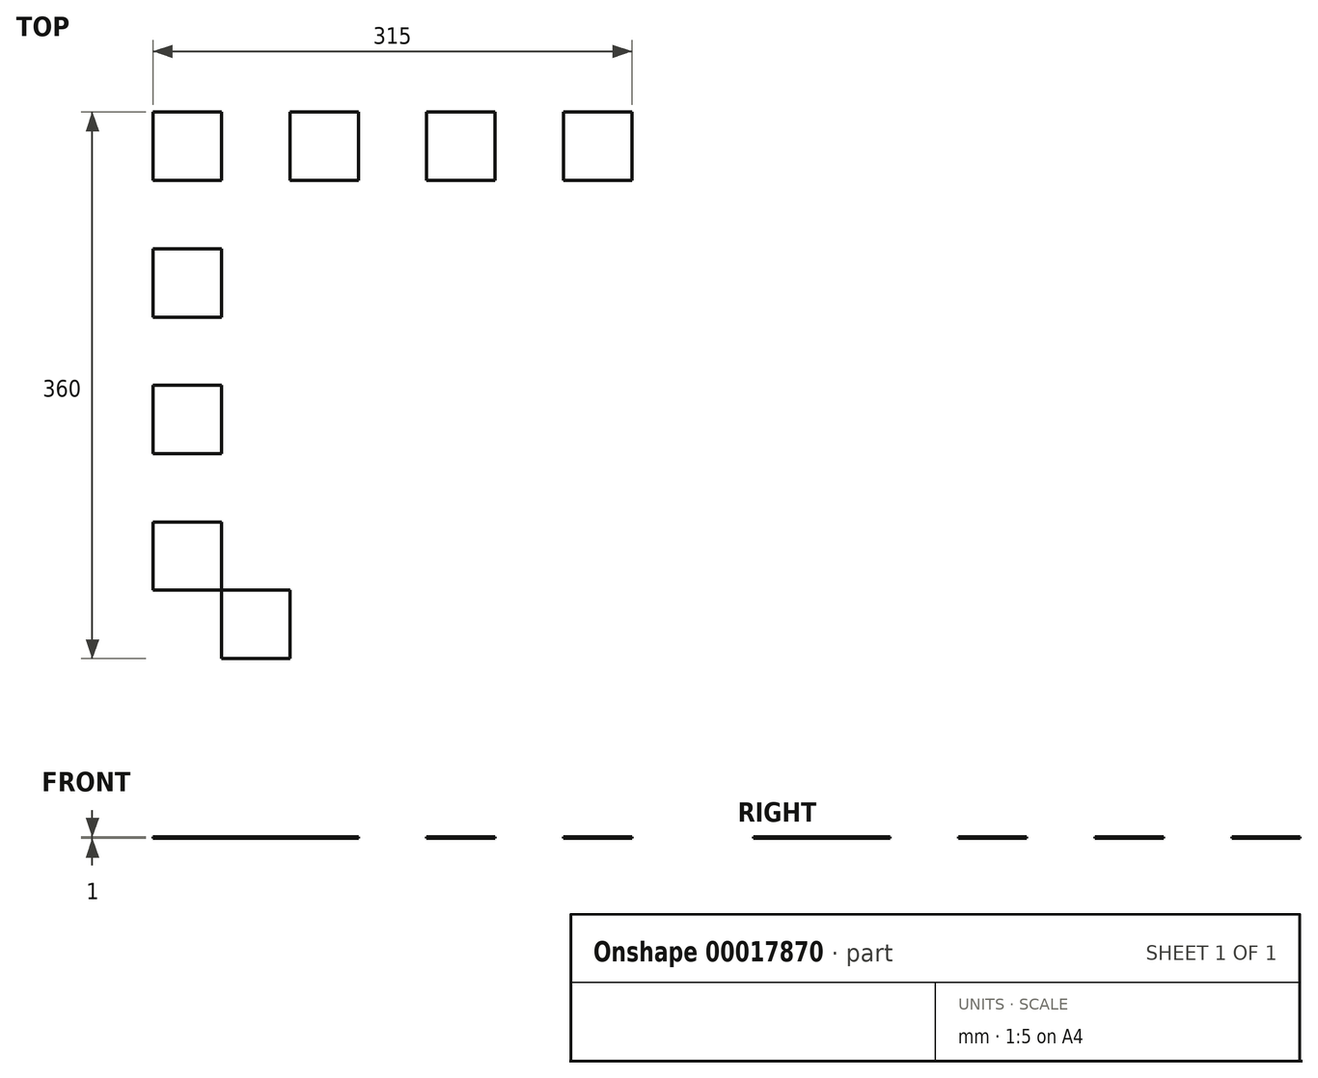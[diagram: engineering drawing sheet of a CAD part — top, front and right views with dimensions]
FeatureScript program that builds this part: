
annotation { "Feature Type Name" : "Feature", "Feature Type Description" : "" }
export const myFeature = defineFeature(function(context is Context, id is Id, definition is map)
    precondition{}
    {
        {
            var Q0;
            Q0=qCreatedBy(makeId("Top.planeOp"),FACE);
            var sketch = newSketch(context, id + "F0", { "sketchPlane" : qUnion([Q0])});
            skLineSegment(sketch, "E0.bottom", {"start": v(0, 0) * mm, "end": v(25.4, 0) * mm});
            skLineSegment(sketch, "E0.top", {"start": v(0, 25.4) * mm, "end": v(25.4, 25.4) * mm});
            skLineSegment(sketch, "E0.left", {"start": v(0, 0) * mm, "end": v(0, 25.4) * mm});
            skLineSegment(sketch, "E0.right", {"start": v(25.4, 0) * mm, "end": v(25.4, 25.4) * mm});
            skSolve(sketch);
        }
        {
            var Q0;
            Q0=qCreatedBy(makeId("Top.planeOp"),FACE);
            var sketch = newSketch(context, id + "F1", { "sketchPlane" : qUnion([Q0])});
            skLineSegment(sketch, "E1.bottom", {"start": v(-9.8, -9.8) * mm, "end": v(35.2, -9.8) * mm});
            skLineSegment(sketch, "E1.top", {"start": v(-9.8, 35.2) * mm, "end": v(35.2, 35.2) * mm});
            skLineSegment(sketch, "E1.left", {"start": v(-9.8, -9.8) * mm, "end": v(-9.8, 35.2) * mm});
            skLineSegment(sketch, "E1.right", {"start": v(35.2, -9.8) * mm, "end": v(35.2, 35.2) * mm});
            skLineSegment(sketch, "E2.0.1.0", {"start": v(-9.8, 80.2) * mm, "end": v(35.2, 80.2) * mm});
            skLineSegment(sketch, "E2.0.1.1", {"start": v(-9.8, 35.2) * mm, "end": v(-9.8, 80.2) * mm});
            skLineSegment(sketch, "E2.0.1.3", {"start": v(35.2, 35.2) * mm, "end": v(35.2, 80.2) * mm});
            skLineSegment(sketch, "E2.0.2.0", {"start": v(-9.8, 125.2) * mm, "end": v(35.2, 125.2) * mm});
            skLineSegment(sketch, "E2.0.2.1", {"start": v(-9.8, 80.2) * mm, "end": v(-9.8, 125.2) * mm});
            skLineSegment(sketch, "E2.0.2.2", {"start": v(-9.8, 80.2) * mm, "end": v(35.2, 80.2) * mm});
            skLineSegment(sketch, "E2.0.2.3", {"start": v(35.2, 80.2) * mm, "end": v(35.2, 125.2) * mm});
            skLineSegment(sketch, "E2.0.3.0", {"start": v(-9.8, 170.2) * mm, "end": v(35.2, 170.2) * mm});
            skLineSegment(sketch, "E2.0.3.1", {"start": v(-9.8, 125.2) * mm, "end": v(-9.8, 170.2) * mm});
            skLineSegment(sketch, "E2.0.3.2", {"start": v(-9.8, 125.2) * mm, "end": v(35.2, 125.2) * mm});
            skLineSegment(sketch, "E2.0.3.3", {"start": v(35.2, 125.2) * mm, "end": v(35.2, 170.2) * mm});
            skLineSegment(sketch, "E2.0.4.0", {"start": v(-9.8, 215.2) * mm, "end": v(35.2, 215.2) * mm});
            skLineSegment(sketch, "E2.0.4.1", {"start": v(-9.8, 170.2) * mm, "end": v(-9.8, 215.2) * mm});
            skLineSegment(sketch, "E2.0.4.2", {"start": v(-9.8, 170.2) * mm, "end": v(35.2, 170.2) * mm});
            skLineSegment(sketch, "E2.0.4.3", {"start": v(35.2, 170.2) * mm, "end": v(35.2, 215.2) * mm});
            skLineSegment(sketch, "E2.0.5.0", {"start": v(-9.8, 260.2) * mm, "end": v(35.2, 260.2) * mm});
            skLineSegment(sketch, "E2.0.5.1", {"start": v(-9.8, 215.2) * mm, "end": v(-9.8, 260.2) * mm});
            skLineSegment(sketch, "E2.0.5.2", {"start": v(-9.8, 215.2) * mm, "end": v(35.2, 215.2) * mm});
            skLineSegment(sketch, "E2.0.5.3", {"start": v(35.2, 215.2) * mm, "end": v(35.2, 260.2) * mm});
            skLineSegment(sketch, "E2.0.6.0", {"start": v(-9.8, 305.2) * mm, "end": v(35.2, 305.2) * mm});
            skLineSegment(sketch, "E2.0.6.1", {"start": v(-9.8, 260.2) * mm, "end": v(-9.8, 305.2) * mm});
            skLineSegment(sketch, "E2.0.6.2", {"start": v(-9.8, 260.2) * mm, "end": v(35.2, 260.2) * mm});
            skLineSegment(sketch, "E2.0.6.3", {"start": v(35.2, 260.2) * mm, "end": v(35.2, 305.2) * mm});
            skLineSegment(sketch, "E2.0.7.0", {"start": v(-9.8, 350.2) * mm, "end": v(35.2, 350.2) * mm});
            skLineSegment(sketch, "E2.0.7.1", {"start": v(-9.8, 305.2) * mm, "end": v(-9.8, 350.2) * mm});
            skLineSegment(sketch, "E2.0.7.2", {"start": v(-9.8, 305.2) * mm, "end": v(35.2, 305.2) * mm});
            skLineSegment(sketch, "E2.0.7.3", {"start": v(35.2, 305.2) * mm, "end": v(35.2, 350.2) * mm});
            skLineSegment(sketch, "E2.1.0.0", {"start": v(35.2, 35.2) * mm, "end": v(80.2, 35.2) * mm});
            skLineSegment(sketch, "E2.1.0.2", {"start": v(35.2, -9.8) * mm, "end": v(80.2, -9.8) * mm});
            skLineSegment(sketch, "E2.1.0.3", {"start": v(80.2, -9.8) * mm, "end": v(80.2, 35.2) * mm});
            skLineSegment(sketch, "E2.1.1.0", {"start": v(35.2, 80.2) * mm, "end": v(80.2, 80.2) * mm});
            skLineSegment(sketch, "E2.1.1.1", {"start": v(35.2, 35.2) * mm, "end": v(35.2, 80.2) * mm});
            skLineSegment(sketch, "E2.1.1.2", {"start": v(35.2, 35.2) * mm, "end": v(80.2, 35.2) * mm});
            skLineSegment(sketch, "E2.1.1.3", {"start": v(80.2, 35.2) * mm, "end": v(80.2, 80.2) * mm});
            skLineSegment(sketch, "E2.1.2.0", {"start": v(35.2, 125.2) * mm, "end": v(80.2, 125.2) * mm});
            skLineSegment(sketch, "E2.1.2.1", {"start": v(35.2, 80.2) * mm, "end": v(35.2, 125.2) * mm});
            skLineSegment(sketch, "E2.1.2.2", {"start": v(35.2, 80.2) * mm, "end": v(80.2, 80.2) * mm});
            skLineSegment(sketch, "E2.1.2.3", {"start": v(80.2, 80.2) * mm, "end": v(80.2, 125.2) * mm});
            skLineSegment(sketch, "E2.1.3.0", {"start": v(35.2, 170.2) * mm, "end": v(80.2, 170.2) * mm});
            skLineSegment(sketch, "E2.1.3.1", {"start": v(35.2, 125.2) * mm, "end": v(35.2, 170.2) * mm});
            skLineSegment(sketch, "E2.1.3.2", {"start": v(35.2, 125.2) * mm, "end": v(80.2, 125.2) * mm});
            skLineSegment(sketch, "E2.1.3.3", {"start": v(80.2, 125.2) * mm, "end": v(80.2, 170.2) * mm});
            skLineSegment(sketch, "E2.1.4.0", {"start": v(35.2, 215.2) * mm, "end": v(80.2, 215.2) * mm});
            skLineSegment(sketch, "E2.1.4.1", {"start": v(35.2, 170.2) * mm, "end": v(35.2, 215.2) * mm});
            skLineSegment(sketch, "E2.1.4.2", {"start": v(35.2, 170.2) * mm, "end": v(80.2, 170.2) * mm});
            skLineSegment(sketch, "E2.1.4.3", {"start": v(80.2, 170.2) * mm, "end": v(80.2, 215.2) * mm});
            skLineSegment(sketch, "E2.1.5.0", {"start": v(35.2, 260.2) * mm, "end": v(80.2, 260.2) * mm});
            skLineSegment(sketch, "E2.1.5.1", {"start": v(35.2, 215.2) * mm, "end": v(35.2, 260.2) * mm});
            skLineSegment(sketch, "E2.1.5.2", {"start": v(35.2, 215.2) * mm, "end": v(80.2, 215.2) * mm});
            skLineSegment(sketch, "E2.1.5.3", {"start": v(80.2, 215.2) * mm, "end": v(80.2, 260.2) * mm});
            skLineSegment(sketch, "E2.1.6.0", {"start": v(35.2, 305.2) * mm, "end": v(80.2, 305.2) * mm});
            skLineSegment(sketch, "E2.1.6.1", {"start": v(35.2, 260.2) * mm, "end": v(35.2, 305.2) * mm});
            skLineSegment(sketch, "E2.1.6.2", {"start": v(35.2, 260.2) * mm, "end": v(80.2, 260.2) * mm});
            skLineSegment(sketch, "E2.1.6.3", {"start": v(80.2, 260.2) * mm, "end": v(80.2, 305.2) * mm});
            skLineSegment(sketch, "E2.1.7.0", {"start": v(35.2, 350.2) * mm, "end": v(80.2, 350.2) * mm});
            skLineSegment(sketch, "E2.1.7.1", {"start": v(35.2, 305.2) * mm, "end": v(35.2, 350.2) * mm});
            skLineSegment(sketch, "E2.1.7.2", {"start": v(35.2, 305.2) * mm, "end": v(80.2, 305.2) * mm});
            skLineSegment(sketch, "E2.1.7.3", {"start": v(80.2, 305.2) * mm, "end": v(80.2, 350.2) * mm});
            skLineSegment(sketch, "E2.2.0.0", {"start": v(80.2, 35.2) * mm, "end": v(125.2, 35.2) * mm});
            skLineSegment(sketch, "E2.2.0.1", {"start": v(80.2, -9.8) * mm, "end": v(80.2, 35.2) * mm});
            skLineSegment(sketch, "E2.2.0.2", {"start": v(80.2, -9.8) * mm, "end": v(125.2, -9.8) * mm});
            skLineSegment(sketch, "E2.2.0.3", {"start": v(125.2, -9.8) * mm, "end": v(125.2, 35.2) * mm});
            skLineSegment(sketch, "E2.2.1.0", {"start": v(80.2, 80.2) * mm, "end": v(125.2, 80.2) * mm});
            skLineSegment(sketch, "E2.2.1.1", {"start": v(80.2, 35.2) * mm, "end": v(80.2, 80.2) * mm});
            skLineSegment(sketch, "E2.2.1.2", {"start": v(80.2, 35.2) * mm, "end": v(125.2, 35.2) * mm});
            skLineSegment(sketch, "E2.2.1.3", {"start": v(125.2, 35.2) * mm, "end": v(125.2, 80.2) * mm});
            skLineSegment(sketch, "E2.2.2.0", {"start": v(80.2, 125.2) * mm, "end": v(125.2, 125.2) * mm});
            skLineSegment(sketch, "E2.2.2.1", {"start": v(80.2, 80.2) * mm, "end": v(80.2, 125.2) * mm});
            skLineSegment(sketch, "E2.2.2.2", {"start": v(80.2, 80.2) * mm, "end": v(125.2, 80.2) * mm});
            skLineSegment(sketch, "E2.2.2.3", {"start": v(125.2, 80.2) * mm, "end": v(125.2, 125.2) * mm});
            skLineSegment(sketch, "E2.2.3.0", {"start": v(80.2, 170.2) * mm, "end": v(125.2, 170.2) * mm});
            skLineSegment(sketch, "E2.2.3.1", {"start": v(80.2, 125.2) * mm, "end": v(80.2, 170.2) * mm});
            skLineSegment(sketch, "E2.2.3.2", {"start": v(80.2, 125.2) * mm, "end": v(125.2, 125.2) * mm});
            skLineSegment(sketch, "E2.2.3.3", {"start": v(125.2, 125.2) * mm, "end": v(125.2, 170.2) * mm});
            skLineSegment(sketch, "E2.2.4.0", {"start": v(80.2, 215.2) * mm, "end": v(125.2, 215.2) * mm});
            skLineSegment(sketch, "E2.2.4.1", {"start": v(80.2, 170.2) * mm, "end": v(80.2, 215.2) * mm});
            skLineSegment(sketch, "E2.2.4.2", {"start": v(80.2, 170.2) * mm, "end": v(125.2, 170.2) * mm});
            skLineSegment(sketch, "E2.2.4.3", {"start": v(125.2, 170.2) * mm, "end": v(125.2, 215.2) * mm});
            skLineSegment(sketch, "E2.2.5.0", {"start": v(80.2, 260.2) * mm, "end": v(125.2, 260.2) * mm});
            skLineSegment(sketch, "E2.2.5.1", {"start": v(80.2, 215.2) * mm, "end": v(80.2, 260.2) * mm});
            skLineSegment(sketch, "E2.2.5.2", {"start": v(80.2, 215.2) * mm, "end": v(125.2, 215.2) * mm});
            skLineSegment(sketch, "E2.2.5.3", {"start": v(125.2, 215.2) * mm, "end": v(125.2, 260.2) * mm});
            skLineSegment(sketch, "E2.2.6.0", {"start": v(80.2, 305.2) * mm, "end": v(125.2, 305.2) * mm});
            skLineSegment(sketch, "E2.2.6.1", {"start": v(80.2, 260.2) * mm, "end": v(80.2, 305.2) * mm});
            skLineSegment(sketch, "E2.2.6.2", {"start": v(80.2, 260.2) * mm, "end": v(125.2, 260.2) * mm});
            skLineSegment(sketch, "E2.2.6.3", {"start": v(125.2, 260.2) * mm, "end": v(125.2, 305.2) * mm});
            skLineSegment(sketch, "E2.2.7.0", {"start": v(80.2, 350.2) * mm, "end": v(125.2, 350.2) * mm});
            skLineSegment(sketch, "E2.2.7.1", {"start": v(80.2, 305.2) * mm, "end": v(80.2, 350.2) * mm});
            skLineSegment(sketch, "E2.2.7.2", {"start": v(80.2, 305.2) * mm, "end": v(125.2, 305.2) * mm});
            skLineSegment(sketch, "E2.2.7.3", {"start": v(125.2, 305.2) * mm, "end": v(125.2, 350.2) * mm});
            skLineSegment(sketch, "E2.3.0.0", {"start": v(125.2, 35.2) * mm, "end": v(170.2, 35.2) * mm});
            skLineSegment(sketch, "E2.3.0.1", {"start": v(125.2, -9.8) * mm, "end": v(125.2, 35.2) * mm});
            skLineSegment(sketch, "E2.3.0.2", {"start": v(125.2, -9.8) * mm, "end": v(170.2, -9.8) * mm});
            skLineSegment(sketch, "E2.3.0.3", {"start": v(170.2, -9.8) * mm, "end": v(170.2, 35.2) * mm});
            skLineSegment(sketch, "E2.3.1.0", {"start": v(125.2, 80.2) * mm, "end": v(170.2, 80.2) * mm});
            skLineSegment(sketch, "E2.3.1.1", {"start": v(125.2, 35.2) * mm, "end": v(125.2, 80.2) * mm});
            skLineSegment(sketch, "E2.3.1.2", {"start": v(125.2, 35.2) * mm, "end": v(170.2, 35.2) * mm});
            skLineSegment(sketch, "E2.3.1.3", {"start": v(170.2, 35.2) * mm, "end": v(170.2, 80.2) * mm});
            skLineSegment(sketch, "E2.3.2.0", {"start": v(125.2, 125.2) * mm, "end": v(170.2, 125.2) * mm});
            skLineSegment(sketch, "E2.3.2.1", {"start": v(125.2, 80.2) * mm, "end": v(125.2, 125.2) * mm});
            skLineSegment(sketch, "E2.3.2.2", {"start": v(125.2, 80.2) * mm, "end": v(170.2, 80.2) * mm});
            skLineSegment(sketch, "E2.3.2.3", {"start": v(170.2, 80.2) * mm, "end": v(170.2, 125.2) * mm});
            skLineSegment(sketch, "E2.3.3.0", {"start": v(125.2, 170.2) * mm, "end": v(170.2, 170.2) * mm});
            skLineSegment(sketch, "E2.3.3.1", {"start": v(125.2, 125.2) * mm, "end": v(125.2, 170.2) * mm});
            skLineSegment(sketch, "E2.3.3.2", {"start": v(125.2, 125.2) * mm, "end": v(170.2, 125.2) * mm});
            skLineSegment(sketch, "E2.3.3.3", {"start": v(170.2, 125.2) * mm, "end": v(170.2, 170.2) * mm});
            skLineSegment(sketch, "E2.3.4.0", {"start": v(125.2, 215.2) * mm, "end": v(170.2, 215.2) * mm});
            skLineSegment(sketch, "E2.3.4.1", {"start": v(125.2, 170.2) * mm, "end": v(125.2, 215.2) * mm});
            skLineSegment(sketch, "E2.3.4.2", {"start": v(125.2, 170.2) * mm, "end": v(170.2, 170.2) * mm});
            skLineSegment(sketch, "E2.3.4.3", {"start": v(170.2, 170.2) * mm, "end": v(170.2, 215.2) * mm});
            skLineSegment(sketch, "E2.3.5.0", {"start": v(125.2, 260.2) * mm, "end": v(170.2, 260.2) * mm});
            skLineSegment(sketch, "E2.3.5.1", {"start": v(125.2, 215.2) * mm, "end": v(125.2, 260.2) * mm});
            skLineSegment(sketch, "E2.3.5.2", {"start": v(125.2, 215.2) * mm, "end": v(170.2, 215.2) * mm});
            skLineSegment(sketch, "E2.3.5.3", {"start": v(170.2, 215.2) * mm, "end": v(170.2, 260.2) * mm});
            skLineSegment(sketch, "E2.3.6.0", {"start": v(125.2, 305.2) * mm, "end": v(170.2, 305.2) * mm});
            skLineSegment(sketch, "E2.3.6.1", {"start": v(125.2, 260.2) * mm, "end": v(125.2, 305.2) * mm});
            skLineSegment(sketch, "E2.3.6.2", {"start": v(125.2, 260.2) * mm, "end": v(170.2, 260.2) * mm});
            skLineSegment(sketch, "E2.3.6.3", {"start": v(170.2, 260.2) * mm, "end": v(170.2, 305.2) * mm});
            skLineSegment(sketch, "E2.3.7.0", {"start": v(125.2, 350.2) * mm, "end": v(170.2, 350.2) * mm});
            skLineSegment(sketch, "E2.3.7.1", {"start": v(125.2, 305.2) * mm, "end": v(125.2, 350.2) * mm});
            skLineSegment(sketch, "E2.3.7.2", {"start": v(125.2, 305.2) * mm, "end": v(170.2, 305.2) * mm});
            skLineSegment(sketch, "E2.3.7.3", {"start": v(170.2, 305.2) * mm, "end": v(170.2, 350.2) * mm});
            skLineSegment(sketch, "E2.4.0.0", {"start": v(170.2, 35.2) * mm, "end": v(215.2, 35.2) * mm});
            skLineSegment(sketch, "E2.4.0.1", {"start": v(170.2, -9.8) * mm, "end": v(170.2, 35.2) * mm});
            skLineSegment(sketch, "E2.4.0.2", {"start": v(170.2, -9.8) * mm, "end": v(215.2, -9.8) * mm});
            skLineSegment(sketch, "E2.4.0.3", {"start": v(215.2, -9.8) * mm, "end": v(215.2, 35.2) * mm});
            skLineSegment(sketch, "E2.4.1.0", {"start": v(170.2, 80.2) * mm, "end": v(215.2, 80.2) * mm});
            skLineSegment(sketch, "E2.4.1.1", {"start": v(170.2, 35.2) * mm, "end": v(170.2, 80.2) * mm});
            skLineSegment(sketch, "E2.4.1.2", {"start": v(170.2, 35.2) * mm, "end": v(215.2, 35.2) * mm});
            skLineSegment(sketch, "E2.4.1.3", {"start": v(215.2, 35.2) * mm, "end": v(215.2, 80.2) * mm});
            skLineSegment(sketch, "E2.4.2.0", {"start": v(170.2, 125.2) * mm, "end": v(215.2, 125.2) * mm});
            skLineSegment(sketch, "E2.4.2.1", {"start": v(170.2, 80.2) * mm, "end": v(170.2, 125.2) * mm});
            skLineSegment(sketch, "E2.4.2.2", {"start": v(170.2, 80.2) * mm, "end": v(215.2, 80.2) * mm});
            skLineSegment(sketch, "E2.4.2.3", {"start": v(215.2, 80.2) * mm, "end": v(215.2, 125.2) * mm});
            skLineSegment(sketch, "E2.4.3.0", {"start": v(170.2, 170.2) * mm, "end": v(215.2, 170.2) * mm});
            skLineSegment(sketch, "E2.4.3.1", {"start": v(170.2, 125.2) * mm, "end": v(170.2, 170.2) * mm});
            skLineSegment(sketch, "E2.4.3.2", {"start": v(170.2, 125.2) * mm, "end": v(215.2, 125.2) * mm});
            skLineSegment(sketch, "E2.4.3.3", {"start": v(215.2, 125.2) * mm, "end": v(215.2, 170.2) * mm});
            skLineSegment(sketch, "E2.4.4.0", {"start": v(170.2, 215.2) * mm, "end": v(215.2, 215.2) * mm});
            skLineSegment(sketch, "E2.4.4.1", {"start": v(170.2, 170.2) * mm, "end": v(170.2, 215.2) * mm});
            skLineSegment(sketch, "E2.4.4.2", {"start": v(170.2, 170.2) * mm, "end": v(215.2, 170.2) * mm});
            skLineSegment(sketch, "E2.4.4.3", {"start": v(215.2, 170.2) * mm, "end": v(215.2, 215.2) * mm});
            skLineSegment(sketch, "E2.4.5.0", {"start": v(170.2, 260.2) * mm, "end": v(215.2, 260.2) * mm});
            skLineSegment(sketch, "E2.4.5.1", {"start": v(170.2, 215.2) * mm, "end": v(170.2, 260.2) * mm});
            skLineSegment(sketch, "E2.4.5.2", {"start": v(170.2, 215.2) * mm, "end": v(215.2, 215.2) * mm});
            skLineSegment(sketch, "E2.4.5.3", {"start": v(215.2, 215.2) * mm, "end": v(215.2, 260.2) * mm});
            skLineSegment(sketch, "E2.4.6.0", {"start": v(170.2, 305.2) * mm, "end": v(215.2, 305.2) * mm});
            skLineSegment(sketch, "E2.4.6.1", {"start": v(170.2, 260.2) * mm, "end": v(170.2, 305.2) * mm});
            skLineSegment(sketch, "E2.4.6.2", {"start": v(170.2, 260.2) * mm, "end": v(215.2, 260.2) * mm});
            skLineSegment(sketch, "E2.4.6.3", {"start": v(215.2, 260.2) * mm, "end": v(215.2, 305.2) * mm});
            skLineSegment(sketch, "E2.4.7.0", {"start": v(170.2, 350.2) * mm, "end": v(215.2, 350.2) * mm});
            skLineSegment(sketch, "E2.4.7.1", {"start": v(170.2, 305.2) * mm, "end": v(170.2, 350.2) * mm});
            skLineSegment(sketch, "E2.4.7.2", {"start": v(170.2, 305.2) * mm, "end": v(215.2, 305.2) * mm});
            skLineSegment(sketch, "E2.4.7.3", {"start": v(215.2, 305.2) * mm, "end": v(215.2, 350.2) * mm});
            skLineSegment(sketch, "E2.5.0.0", {"start": v(215.2, 35.2) * mm, "end": v(260.2, 35.2) * mm});
            skLineSegment(sketch, "E2.5.0.1", {"start": v(215.2, -9.8) * mm, "end": v(215.2, 35.2) * mm});
            skLineSegment(sketch, "E2.5.0.2", {"start": v(215.2, -9.8) * mm, "end": v(260.2, -9.8) * mm});
            skLineSegment(sketch, "E2.5.0.3", {"start": v(260.2, -9.8) * mm, "end": v(260.2, 35.2) * mm});
            skLineSegment(sketch, "E2.5.1.0", {"start": v(215.2, 80.2) * mm, "end": v(260.2, 80.2) * mm});
            skLineSegment(sketch, "E2.5.1.1", {"start": v(215.2, 35.2) * mm, "end": v(215.2, 80.2) * mm});
            skLineSegment(sketch, "E2.5.1.2", {"start": v(215.2, 35.2) * mm, "end": v(260.2, 35.2) * mm});
            skLineSegment(sketch, "E2.5.1.3", {"start": v(260.2, 35.2) * mm, "end": v(260.2, 80.2) * mm});
            skLineSegment(sketch, "E2.5.2.0", {"start": v(215.2, 125.2) * mm, "end": v(260.2, 125.2) * mm});
            skLineSegment(sketch, "E2.5.2.1", {"start": v(215.2, 80.2) * mm, "end": v(215.2, 125.2) * mm});
            skLineSegment(sketch, "E2.5.2.2", {"start": v(215.2, 80.2) * mm, "end": v(260.2, 80.2) * mm});
            skLineSegment(sketch, "E2.5.2.3", {"start": v(260.2, 80.2) * mm, "end": v(260.2, 125.2) * mm});
            skLineSegment(sketch, "E2.5.3.0", {"start": v(215.2, 170.2) * mm, "end": v(260.2, 170.2) * mm});
            skLineSegment(sketch, "E2.5.3.1", {"start": v(215.2, 125.2) * mm, "end": v(215.2, 170.2) * mm});
            skLineSegment(sketch, "E2.5.3.2", {"start": v(215.2, 125.2) * mm, "end": v(260.2, 125.2) * mm});
            skLineSegment(sketch, "E2.5.3.3", {"start": v(260.2, 125.2) * mm, "end": v(260.2, 170.2) * mm});
            skLineSegment(sketch, "E2.5.4.0", {"start": v(215.2, 215.2) * mm, "end": v(260.2, 215.2) * mm});
            skLineSegment(sketch, "E2.5.4.1", {"start": v(215.2, 170.2) * mm, "end": v(215.2, 215.2) * mm});
            skLineSegment(sketch, "E2.5.4.2", {"start": v(215.2, 170.2) * mm, "end": v(260.2, 170.2) * mm});
            skLineSegment(sketch, "E2.5.4.3", {"start": v(260.2, 170.2) * mm, "end": v(260.2, 215.2) * mm});
            skLineSegment(sketch, "E2.5.5.0", {"start": v(215.2, 260.2) * mm, "end": v(260.2, 260.2) * mm});
            skLineSegment(sketch, "E2.5.5.1", {"start": v(215.2, 215.2) * mm, "end": v(215.2, 260.2) * mm});
            skLineSegment(sketch, "E2.5.5.2", {"start": v(215.2, 215.2) * mm, "end": v(260.2, 215.2) * mm});
            skLineSegment(sketch, "E2.5.5.3", {"start": v(260.2, 215.2) * mm, "end": v(260.2, 260.2) * mm});
            skLineSegment(sketch, "E2.5.6.0", {"start": v(215.2, 305.2) * mm, "end": v(260.2, 305.2) * mm});
            skLineSegment(sketch, "E2.5.6.1", {"start": v(215.2, 260.2) * mm, "end": v(215.2, 305.2) * mm});
            skLineSegment(sketch, "E2.5.6.2", {"start": v(215.2, 260.2) * mm, "end": v(260.2, 260.2) * mm});
            skLineSegment(sketch, "E2.5.6.3", {"start": v(260.2, 260.2) * mm, "end": v(260.2, 305.2) * mm});
            skLineSegment(sketch, "E2.5.7.0", {"start": v(215.2, 350.2) * mm, "end": v(260.2, 350.2) * mm});
            skLineSegment(sketch, "E2.5.7.1", {"start": v(215.2, 305.2) * mm, "end": v(215.2, 350.2) * mm});
            skLineSegment(sketch, "E2.5.7.2", {"start": v(215.2, 305.2) * mm, "end": v(260.2, 305.2) * mm});
            skLineSegment(sketch, "E2.5.7.3", {"start": v(260.2, 305.2) * mm, "end": v(260.2, 350.2) * mm});
            skLineSegment(sketch, "E2.6.0.0", {"start": v(260.2, 35.2) * mm, "end": v(305.2, 35.2) * mm});
            skLineSegment(sketch, "E2.6.0.1", {"start": v(260.2, -9.8) * mm, "end": v(260.2, 35.2) * mm});
            skLineSegment(sketch, "E2.6.0.2", {"start": v(260.2, -9.8) * mm, "end": v(305.2, -9.8) * mm});
            skLineSegment(sketch, "E2.6.0.3", {"start": v(305.2, -9.8) * mm, "end": v(305.2, 35.2) * mm});
            skLineSegment(sketch, "E2.6.1.0", {"start": v(260.2, 80.2) * mm, "end": v(305.2, 80.2) * mm});
            skLineSegment(sketch, "E2.6.1.1", {"start": v(260.2, 35.2) * mm, "end": v(260.2, 80.2) * mm});
            skLineSegment(sketch, "E2.6.1.2", {"start": v(260.2, 35.2) * mm, "end": v(305.2, 35.2) * mm});
            skLineSegment(sketch, "E2.6.1.3", {"start": v(305.2, 35.2) * mm, "end": v(305.2, 80.2) * mm});
            skLineSegment(sketch, "E2.6.2.0", {"start": v(260.2, 125.2) * mm, "end": v(305.2, 125.2) * mm});
            skLineSegment(sketch, "E2.6.2.1", {"start": v(260.2, 80.2) * mm, "end": v(260.2, 125.2) * mm});
            skLineSegment(sketch, "E2.6.2.2", {"start": v(260.2, 80.2) * mm, "end": v(305.2, 80.2) * mm});
            skLineSegment(sketch, "E2.6.2.3", {"start": v(305.2, 80.2) * mm, "end": v(305.2, 125.2) * mm});
            skLineSegment(sketch, "E2.6.3.0", {"start": v(260.2, 170.2) * mm, "end": v(305.2, 170.2) * mm});
            skLineSegment(sketch, "E2.6.3.1", {"start": v(260.2, 125.2) * mm, "end": v(260.2, 170.2) * mm});
            skLineSegment(sketch, "E2.6.3.2", {"start": v(260.2, 125.2) * mm, "end": v(305.2, 125.2) * mm});
            skLineSegment(sketch, "E2.6.3.3", {"start": v(305.2, 125.2) * mm, "end": v(305.2, 170.2) * mm});
            skLineSegment(sketch, "E2.6.4.0", {"start": v(260.2, 215.2) * mm, "end": v(305.2, 215.2) * mm});
            skLineSegment(sketch, "E2.6.4.1", {"start": v(260.2, 170.2) * mm, "end": v(260.2, 215.2) * mm});
            skLineSegment(sketch, "E2.6.4.2", {"start": v(260.2, 170.2) * mm, "end": v(305.2, 170.2) * mm});
            skLineSegment(sketch, "E2.6.4.3", {"start": v(305.2, 170.2) * mm, "end": v(305.2, 215.2) * mm});
            skLineSegment(sketch, "E2.6.5.0", {"start": v(260.2, 260.2) * mm, "end": v(305.2, 260.2) * mm});
            skLineSegment(sketch, "E2.6.5.1", {"start": v(260.2, 215.2) * mm, "end": v(260.2, 260.2) * mm});
            skLineSegment(sketch, "E2.6.5.2", {"start": v(260.2, 215.2) * mm, "end": v(305.2, 215.2) * mm});
            skLineSegment(sketch, "E2.6.5.3", {"start": v(305.2, 215.2) * mm, "end": v(305.2, 260.2) * mm});
            skLineSegment(sketch, "E2.6.6.0", {"start": v(260.2, 305.2) * mm, "end": v(305.2, 305.2) * mm});
            skLineSegment(sketch, "E2.6.6.1", {"start": v(260.2, 260.2) * mm, "end": v(260.2, 305.2) * mm});
            skLineSegment(sketch, "E2.6.6.2", {"start": v(260.2, 260.2) * mm, "end": v(305.2, 260.2) * mm});
            skLineSegment(sketch, "E2.6.6.3", {"start": v(305.2, 260.2) * mm, "end": v(305.2, 305.2) * mm});
            skLineSegment(sketch, "E2.6.7.0", {"start": v(260.2, 350.2) * mm, "end": v(305.2, 350.2) * mm});
            skLineSegment(sketch, "E2.6.7.1", {"start": v(260.2, 305.2) * mm, "end": v(260.2, 350.2) * mm});
            skLineSegment(sketch, "E2.6.7.2", {"start": v(260.2, 305.2) * mm, "end": v(305.2, 305.2) * mm});
            skLineSegment(sketch, "E2.6.7.3", {"start": v(305.2, 305.2) * mm, "end": v(305.2, 350.2) * mm});
            skLineSegment(sketch, "E2.7.0.0", {"start": v(305.2, 35.2) * mm, "end": v(350.2, 35.2) * mm});
            skLineSegment(sketch, "E2.7.0.1", {"start": v(305.2, -9.8) * mm, "end": v(305.2, 35.2) * mm});
            skLineSegment(sketch, "E2.7.0.2", {"start": v(305.2, -9.8) * mm, "end": v(350.2, -9.8) * mm});
            skLineSegment(sketch, "E2.7.0.3", {"start": v(350.2, -9.8) * mm, "end": v(350.2, 35.2) * mm});
            skLineSegment(sketch, "E2.7.1.0", {"start": v(305.2, 80.2) * mm, "end": v(350.2, 80.2) * mm});
            skLineSegment(sketch, "E2.7.1.1", {"start": v(305.2, 35.2) * mm, "end": v(305.2, 80.2) * mm});
            skLineSegment(sketch, "E2.7.1.2", {"start": v(305.2, 35.2) * mm, "end": v(350.2, 35.2) * mm});
            skLineSegment(sketch, "E2.7.1.3", {"start": v(350.2, 35.2) * mm, "end": v(350.2, 80.2) * mm});
            skLineSegment(sketch, "E2.7.2.0", {"start": v(305.2, 125.2) * mm, "end": v(350.2, 125.2) * mm});
            skLineSegment(sketch, "E2.7.2.1", {"start": v(305.2, 80.2) * mm, "end": v(305.2, 125.2) * mm});
            skLineSegment(sketch, "E2.7.2.2", {"start": v(305.2, 80.2) * mm, "end": v(350.2, 80.2) * mm});
            skLineSegment(sketch, "E2.7.2.3", {"start": v(350.2, 80.2) * mm, "end": v(350.2, 125.2) * mm});
            skLineSegment(sketch, "E2.7.3.0", {"start": v(305.2, 170.2) * mm, "end": v(350.2, 170.2) * mm});
            skLineSegment(sketch, "E2.7.3.1", {"start": v(305.2, 125.2) * mm, "end": v(305.2, 170.2) * mm});
            skLineSegment(sketch, "E2.7.3.2", {"start": v(305.2, 125.2) * mm, "end": v(350.2, 125.2) * mm});
            skLineSegment(sketch, "E2.7.3.3", {"start": v(350.2, 125.2) * mm, "end": v(350.2, 170.2) * mm});
            skLineSegment(sketch, "E2.7.4.0", {"start": v(305.2, 215.2) * mm, "end": v(350.2, 215.2) * mm});
            skLineSegment(sketch, "E2.7.4.1", {"start": v(305.2, 170.2) * mm, "end": v(305.2, 215.2) * mm});
            skLineSegment(sketch, "E2.7.4.2", {"start": v(305.2, 170.2) * mm, "end": v(350.2, 170.2) * mm});
            skLineSegment(sketch, "E2.7.4.3", {"start": v(350.2, 170.2) * mm, "end": v(350.2, 215.2) * mm});
            skLineSegment(sketch, "E2.7.5.0", {"start": v(305.2, 260.2) * mm, "end": v(350.2, 260.2) * mm});
            skLineSegment(sketch, "E2.7.5.1", {"start": v(305.2, 215.2) * mm, "end": v(305.2, 260.2) * mm});
            skLineSegment(sketch, "E2.7.5.2", {"start": v(305.2, 215.2) * mm, "end": v(350.2, 215.2) * mm});
            skLineSegment(sketch, "E2.7.5.3", {"start": v(350.2, 215.2) * mm, "end": v(350.2, 260.2) * mm});
            skLineSegment(sketch, "E2.7.6.0", {"start": v(305.2, 305.2) * mm, "end": v(350.2, 305.2) * mm});
            skLineSegment(sketch, "E2.7.6.1", {"start": v(305.2, 260.2) * mm, "end": v(305.2, 305.2) * mm});
            skLineSegment(sketch, "E2.7.6.2", {"start": v(305.2, 260.2) * mm, "end": v(350.2, 260.2) * mm});
            skLineSegment(sketch, "E2.7.6.3", {"start": v(350.2, 260.2) * mm, "end": v(350.2, 305.2) * mm});
            skLineSegment(sketch, "E2.7.7.0", {"start": v(305.2, 350.2) * mm, "end": v(350.2, 350.2) * mm});
            skLineSegment(sketch, "E2.7.7.1", {"start": v(305.2, 305.2) * mm, "end": v(305.2, 350.2) * mm});
            skLineSegment(sketch, "E2.7.7.2", {"start": v(305.2, 305.2) * mm, "end": v(350.2, 305.2) * mm});
            skLineSegment(sketch, "E2.7.7.3", {"start": v(350.2, 305.2) * mm, "end": v(350.2, 350.2) * mm});
            skLineSegment(sketch, "E2.direction1", {"start": v(-9.8, 35.2) * mm, "end": v(35.2, 35.2) * mm, "construction": true});
            skLineSegment(sketch, "E2.direction2", {"start": v(-9.8, 35.2) * mm, "end": v(-9.8, 80.2) * mm, "construction": true});
            skSolve(sketch);
        }
        {
            var Q0;
            Q0=makeQuery(id+"F1.imprint","IMPRINT",FACE,{"disambiguationData":[TD([[makeQuery(id+"F1.imprint","IMPRINT",EDGE,{"derivedFrom":sQuery(id+"F1.wireOp",EDGE,"E2.7.0.1")}),-1.0]])]});
            var Q1;
            Q1=makeQuery(id+"F1.imprint","IMPRINT",FACE,{"disambiguationData":[TD([[makeQuery(id+"F1.imprint","IMPRINT",EDGE,{"derivedFrom":sQuery(id+"F1.wireOp",EDGE,"E2.6.1.1")}),-1.0]])]});
            var Q2;
            Q2=makeQuery(id+"F1.imprint","IMPRINT",FACE,{"disambiguationData":[TD([[makeQuery(id+"F1.imprint","IMPRINT",EDGE,{"derivedFrom":sQuery(id+"F1.wireOp",EDGE,"E2.5.2.1")}),-1.0]])]});
            var Q3;
            Q3=makeQuery(id+"F1.imprint","IMPRINT",FACE,{"disambiguationData":[TD([[makeQuery(id+"F1.imprint","IMPRINT",EDGE,{"derivedFrom":sQuery(id+"F1.wireOp",EDGE,"E2.4.3.1")}),-1.0]])]});
            var Q4;
            Q4=makeQuery(id+"F1.imprint","IMPRINT",FACE,{"disambiguationData":[TD([[makeQuery(id+"F1.imprint","IMPRINT",EDGE,{"derivedFrom":sQuery(id+"F1.wireOp",EDGE,"E2.3.4.1")}),-1.0]])]});
            var Q5;
            Q5=makeQuery(id+"F1.imprint","IMPRINT",FACE,{"disambiguationData":[TD([[makeQuery(id+"F1.imprint","IMPRINT",EDGE,{"derivedFrom":sQuery(id+"F1.wireOp",EDGE,"E2.2.5.1")}),-1.0]])]});
            var Q6;
            Q6=makeQuery(id+"F1.imprint","IMPRINT",FACE,{"disambiguationData":[TD([[makeQuery(id+"F1.imprint","IMPRINT",EDGE,{"derivedFrom":sQuery(id+"F1.wireOp",EDGE,"E2.1.6.1")}),-1.0]])]});
            var Q7;
            Q7=makeQuery(id+"F1.imprint","IMPRINT",FACE,{"disambiguationData":[TD([[makeQuery(id+"F1.imprint","IMPRINT",EDGE,{"derivedFrom":sQuery(id+"F1.wireOp",EDGE,"E2.0.7.0")}),-1.0]])]});
            var Q8;
            Q8=makeQuery(id+"F1.imprint","IMPRINT",FACE,{"disambiguationData":[TD([[makeQuery(id+"F1.imprint","IMPRINT",EDGE,{"derivedFrom":sQuery(id+"F1.wireOp",EDGE,"E2.2.7.0")}),-1.0]])]});
            var Q9;
            Q9=makeQuery(id+"F1.imprint","IMPRINT",FACE,{"disambiguationData":[TD([[makeQuery(id+"F1.imprint","IMPRINT",EDGE,{"derivedFrom":sQuery(id+"F1.wireOp",EDGE,"E2.4.7.0")}),-1.0]])]});
            var Q10;
            Q10=makeQuery(id+"F1.imprint","IMPRINT",FACE,{"disambiguationData":[TD([[makeQuery(id+"F1.imprint","IMPRINT",EDGE,{"derivedFrom":sQuery(id+"F1.wireOp",EDGE,"E2.6.7.0")}),-1.0]])]});
            var Q11;
            Q11=makeQuery(id+"F1.imprint","IMPRINT",FACE,{"disambiguationData":[TD([[makeQuery(id+"F1.imprint","IMPRINT",EDGE,{"derivedFrom":sQuery(id+"F1.wireOp",EDGE,"E2.7.6.1")}),-1.0]])]});
            var Q12;
            Q12=makeQuery(id+"F1.imprint","IMPRINT",FACE,{"disambiguationData":[TD([[makeQuery(id+"F1.imprint","IMPRINT",EDGE,{"derivedFrom":sQuery(id+"F1.wireOp",EDGE,"E2.3.6.1")}),-1.0]])]});
            var Q13;
            Q13=makeQuery(id+"F1.imprint","IMPRINT",FACE,{"disambiguationData":[TD([[makeQuery(id+"F1.imprint","IMPRINT",EDGE,{"derivedFrom":sQuery(id+"F1.wireOp",EDGE,"E2.5.6.1")}),-1.0]])]});
            var Q14;
            Q14=makeQuery(id+"F1.imprint","IMPRINT",FACE,{"disambiguationData":[TD([[makeQuery(id+"F1.imprint","IMPRINT",EDGE,{"derivedFrom":sQuery(id+"F1.wireOp",EDGE,"E2.6.5.1")}),-1.0]])]});
            var Q15;
            Q15=makeQuery(id+"F1.imprint","IMPRINT",FACE,{"disambiguationData":[TD([[makeQuery(id+"F1.imprint","IMPRINT",EDGE,{"derivedFrom":sQuery(id+"F1.wireOp",EDGE,"E2.7.4.1")}),-1.0]])]});
            var Q16;
            Q16=makeQuery(id+"F1.imprint","IMPRINT",FACE,{"disambiguationData":[TD([[makeQuery(id+"F1.imprint","IMPRINT",EDGE,{"derivedFrom":sQuery(id+"F1.wireOp",EDGE,"E2.6.3.1")}),-1.0]])]});
            var Q17;
            Q17=makeQuery(id+"F1.imprint","IMPRINT",FACE,{"disambiguationData":[TD([[makeQuery(id+"F1.imprint","IMPRINT",EDGE,{"derivedFrom":sQuery(id+"F1.wireOp",EDGE,"E2.7.2.1")}),-1.0]])]});
            var Q18;
            Q18=makeQuery(id+"F1.imprint","IMPRINT",FACE,{"disambiguationData":[TD([[makeQuery(id+"F1.imprint","IMPRINT",EDGE,{"derivedFrom":sQuery(id+"F1.wireOp",EDGE,"E2.5.4.1")}),-1.0]])]});
            var Q19;
            Q19=makeQuery(id+"F1.imprint","IMPRINT",FACE,{"disambiguationData":[TD([[makeQuery(id+"F1.imprint","IMPRINT",EDGE,{"derivedFrom":sQuery(id+"F1.wireOp",EDGE,"E2.4.5.1")}),-1.0]])]});
            var Q20;
            Q20=makeQuery(id+"F1.imprint","IMPRINT",FACE,{"disambiguationData":[TD([[makeQuery(id+"F1.imprint","IMPRINT",EDGE,{"derivedFrom":sQuery(id+"F1.wireOp",EDGE,"E2.0.5.1")}),-1.0]])]});
            var Q21;
            Q21=makeQuery(id+"F1.imprint","IMPRINT",FACE,{"disambiguationData":[TD([[makeQuery(id+"F1.imprint","IMPRINT",EDGE,{"derivedFrom":sQuery(id+"F1.wireOp",EDGE,"E2.1.4.1")}),-1.0]])]});
            var Q22;
            Q22=makeQuery(id+"F1.imprint","IMPRINT",FACE,{"disambiguationData":[TD([[makeQuery(id+"F1.imprint","IMPRINT",EDGE,{"derivedFrom":sQuery(id+"F1.wireOp",EDGE,"E2.2.3.1")}),-1.0]])]});
            var Q23;
            Q23=makeQuery(id+"F1.imprint","IMPRINT",FACE,{"disambiguationData":[TD([[makeQuery(id+"F1.imprint","IMPRINT",EDGE,{"derivedFrom":sQuery(id+"F1.wireOp",EDGE,"E2.3.2.1")}),-1.0]])]});
            var Q24;
            Q24=makeQuery(id+"F1.imprint","IMPRINT",FACE,{"disambiguationData":[TD([[makeQuery(id+"F1.imprint","IMPRINT",EDGE,{"derivedFrom":sQuery(id+"F1.wireOp",EDGE,"E2.4.1.1")}),-1.0]])]});
            var Q25;
            Q25=makeQuery(id+"F1.imprint","IMPRINT",FACE,{"disambiguationData":[TD([[makeQuery(id+"F1.imprint","IMPRINT",EDGE,{"derivedFrom":sQuery(id+"F1.wireOp",EDGE,"E2.5.0.1")}),-1.0]])]});
            var Q26;
            Q26=makeQuery(id+"F1.imprint","IMPRINT",FACE,{"disambiguationData":[TD([[makeQuery(id+"F1.imprint","IMPRINT",EDGE,{"derivedFrom":sQuery(id+"F1.wireOp",EDGE,"E2.3.0.1")}),-1.0]])]});
            var Q27;
            Q27=makeQuery(id+"F1.imprint","IMPRINT",FACE,{"disambiguationData":[TD([[makeQuery(id+"F1.imprint","IMPRINT",EDGE,{"derivedFrom":sQuery(id+"F1.wireOp",EDGE,"E1.right")}),-1.0]])]});
            var Q28;
            Q28=makeQuery(id+"F1.imprint","IMPRINT",FACE,{"disambiguationData":[TD([[makeQuery(id+"F1.imprint","IMPRINT",EDGE,{"derivedFrom":sQuery(id+"F1.wireOp",EDGE,"E2.0.1.1")}),-1.0]])]});
            var Q29;
            Q29=makeQuery(id+"F1.imprint","IMPRINT",FACE,{"disambiguationData":[TD([[makeQuery(id+"F1.imprint","IMPRINT",EDGE,{"derivedFrom":sQuery(id+"F1.wireOp",EDGE,"E2.1.2.1")}),-1.0]])]});
            var Q30;
            Q30=makeQuery(id+"F1.imprint","IMPRINT",FACE,{"disambiguationData":[TD([[makeQuery(id+"F1.imprint","IMPRINT",EDGE,{"derivedFrom":sQuery(id+"F1.wireOp",EDGE,"E2.2.1.1")}),-1.0]])]});
            var Q31;
            Q31=makeQuery(id+"F1.imprint","IMPRINT",FACE,{"disambiguationData":[TD([[makeQuery(id+"F1.imprint","IMPRINT",EDGE,{"derivedFrom":sQuery(id+"F1.wireOp",EDGE,"E2.0.3.1")}),-1.0]])]});
            extrude(context, id + "F2", {"entities" : qUnion([Q0, Q1, Q2, Q3, Q4, Q5, Q6, Q7, Q8, Q9, Q10, Q11, Q12, Q13, Q14, Q15, Q16, Q17, Q18, Q19, Q20, Q21, Q22, Q23, Q24, Q25, Q26, Q27, Q28, Q29, Q30, Q31]), "depth" : 1 * mm});
        }
    });
